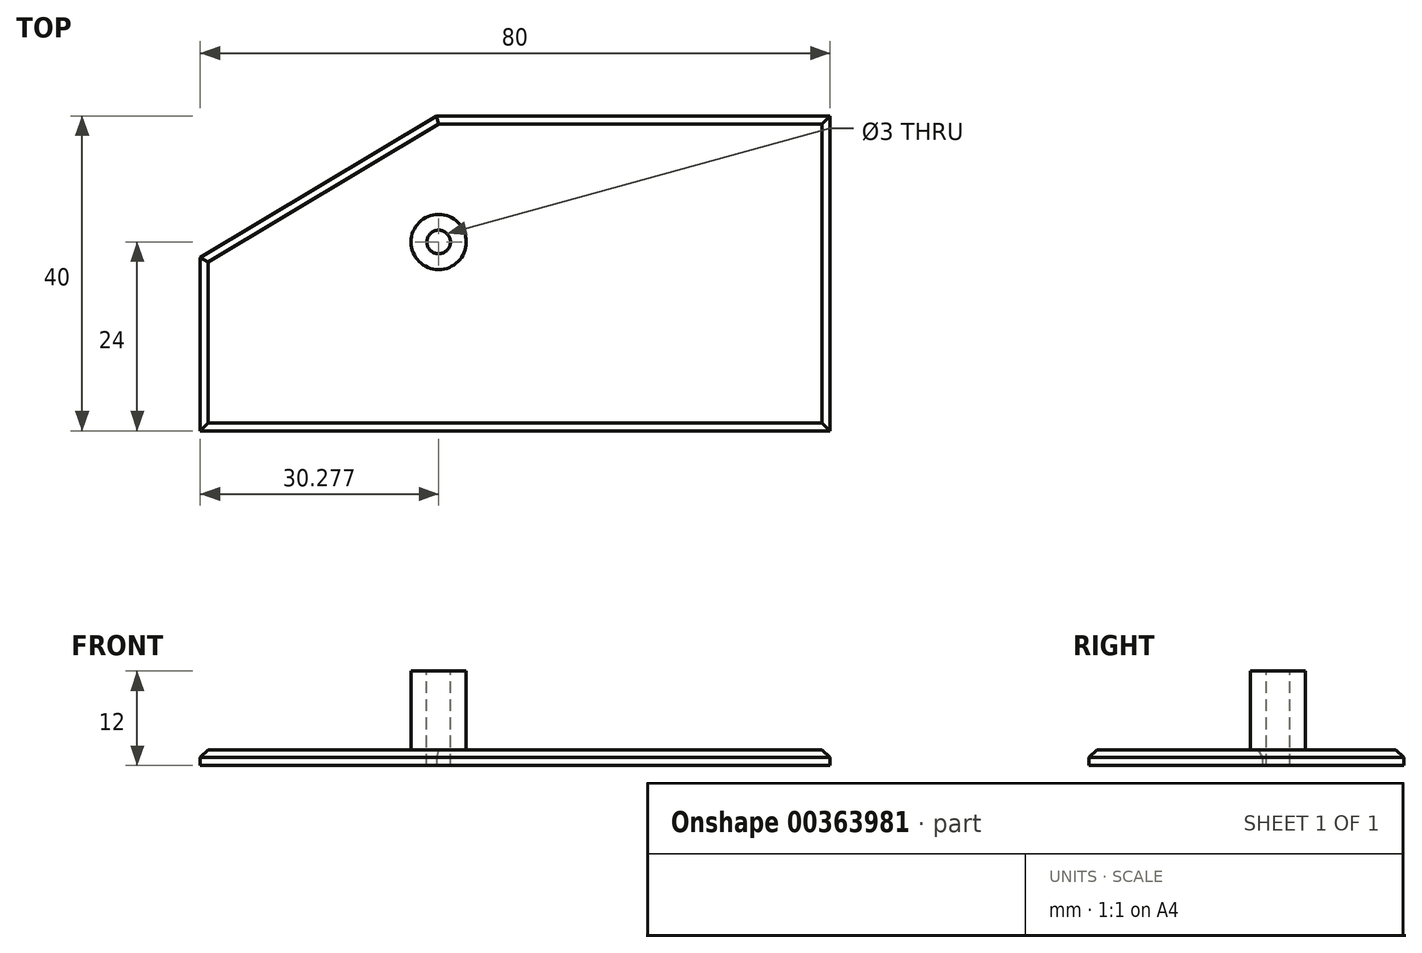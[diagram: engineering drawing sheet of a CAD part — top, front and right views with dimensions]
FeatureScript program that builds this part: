
annotation { "Feature Type Name" : "Feature", "Feature Type Description" : "" }
export const myFeature = defineFeature(function(context is Context, id is Id, definition is map)
    precondition{}
    {
        {
            var Q0;
            Q0=qCreatedBy(makeId("Top.planeOp"),FACE);
            var sketch = newSketch(context, id + "F0", { "sketchPlane" : qUnion([Q0])});
            skLineSegment(sketch, "E0", {"start": v(0, 0) * mm, "end": v(50, 0) * mm});
            skLineSegment(sketch, "E1", {"start": v(0, 0) * mm, "end": v(-30, 0) * mm});
            skLineSegment(sketch, "E2", {"start": v(50, 0) * mm, "end": v(50, 40) * mm});
            skLineSegment(sketch, "E3", {"start": v(50, 40) * mm, "end": v(0, 40) * mm});
            skLineSegment(sketch, "E4", {"start": v(-30, 0) * mm, "end": v(-30, 22) * mm});
            skLineSegment(sketch, "E5", {"start": v(-30, 22) * mm, "end": v(0, 40) * mm});
            skSolve(sketch);
        }
        {
            var Q0;
            Q0=makeQuery(id+"F0.imprint","IMPRINT",FACE,{"disambiguationData":[TD([[makeQuery(id+"F0.imprint","IMPRINT",EDGE,{"derivedFrom":sQuery(id+"F0.wireOp",EDGE,"E0")}),1.0]])]});
            extrude(context, id + "F1", {"entities" : qUnion([Q0]), "depth" : 2 * mm});
        }
        {
            var Q0;
            Q0=makeQuery(id+"F1.opExtrude","CAP_EDGE",EDGE,{"disambiguationData":[OSD([sQuery(id+"F0.wireOp",EDGE,"E0"),sQuery(id+"F0.wireOp",EDGE,"E1")])],"isStart":false});
            var Q1;
            Q1=makeQuery(id+"F1.opExtrude","CAP_EDGE",EDGE,{"disambiguationData":[OSD([sQuery(id+"F0.wireOp",EDGE,"E4")])],"isStart":false});
            var Q2;
            Q2=makeQuery(id+"F1.opExtrude","CAP_EDGE",EDGE,{"disambiguationData":[OSD([sQuery(id+"F0.wireOp",EDGE,"E5")])],"isStart":false});
            var Q3;
            Q3=makeQuery(id+"F1.opExtrude","CAP_EDGE",EDGE,{"disambiguationData":[OSD([sQuery(id+"F0.wireOp",EDGE,"E3")])],"isStart":false});
            var Q4;
            Q4=makeQuery(id+"F1.opExtrude","CAP_EDGE",EDGE,{"disambiguationData":[OSD([sQuery(id+"F0.wireOp",EDGE,"E2")])],"isStart":false});
            chamfer(context, id + "F2", {"entities" : qUnion([Q0, Q1, Q2, Q3, Q4]), "width" : 1 * mm, "tangentPropagation" : true});
        }
        {
            var Q0;
            Q0=makeQuery(id+"F1.opExtrude","CAP_FACE",FACE,{"disambiguationData":[OSD([sQuery(id+"F0.wireOp",EDGE,"E0"),sQuery(id+"F0.wireOp",EDGE,"E1"),sQuery(id+"F0.wireOp",EDGE,"E2"),sQuery(id+"F0.wireOp",EDGE,"E3"),sQuery(id+"F0.wireOp",EDGE,"E4"),sQuery(id+"F0.wireOp",EDGE,"E5")])],"isStart":false});
            var sketch = newSketch(context, id + "F3", { "sketchPlane" : qUnion([Q0])});
            skCircle(sketch, "E6", {"center": v(0.28, 24) * mm, "radius": 3.5 * mm});
            skSolve(sketch);
        }
        {
            var Q0;
            Q0 = qSketchRegion(id + "F3", true);
            extrude(context, id + "F4", {"entities" : qUnion([Q0]), "operationType" : NewBodyOperationType.ADD, "depth" : 10 * mm});
        }
        {
            var Q0;
            Q0=makeQuery(id+"F4.opExtrude","CAP_FACE",FACE,{"disambiguationData":[OSD([sQuery(id+"F3.wireOp",EDGE,"E6")])],"isStart":false});
            var sketch = newSketch(context, id + "F5", { "sketchPlane" : qUnion([Q0])});
            skCircle(sketch, "E7", {"center": v(0.28, 24) * mm, "radius": 1.5 * mm});
            skSolve(sketch);
        }
        {
            var Q0;
            Q0=makeQuery(id+"F5.imprint","IMPRINT",FACE,{"disambiguationData":[TD([[makeQuery(id+"F5.imprint","IMPRINT",EDGE,{"derivedFrom":sQuery(id+"F5.wireOp",EDGE,"E7")}),1.0]])]});
            extrude(context, id + "F6", {"entities" : qUnion([Q0]), "operationType" : NewBodyOperationType.REMOVE, "oppositeDirection" : true, "depth" : 15 * mm});
        }
    });
